# Revit family: P400199-031
name_source: partatom
category: Lighting Fixtures
revit_build: Autodesk Revit 2014 (Build: 20130308_1515(x64)
units: mm (PartAtom-declared; Revit-internal decimal feet)

## types (1)
- P400199-031
    Apparent Load = 60 VA
    Assembly Code = D5020200
    Default Elevation = 48 "
    Description = This versatile chandelier from the Durrell Collection will easily find a home in a variety of settings in need of generous illumination. Light bases reminiscent of vintage candlesticks are coated in a beautiful matte black finish and appear to float around the structure on gently curving metal arms. A wooden column coated in a cerused black finish stretches elegantly at the light fixture’s center to attach the design to a linked metal chain.
    Features = Light bases reminiscent of vintage candlesticks are coated in a beautiful matte black finish.
The light bases appear to float around the structure on gently curving metal arms.
A wooden column coated in a cerused black finish stretches elegantly at the light fixture’s center to attach the design to a linked metal chain.
Ideal for any foyer, hallway, dining room, or kitchen.
Perfect for rustic, farmhouse, and coastal settings.
Measures 26-1/2-inch width by 22-1/2-inch height.
Uses five candelabra base bulbs that are sold separately (60w max - LED or incandescent).
Able to be fully dimmable with dimmable bulbs.
Includes installation instructions and mounting hardware.
Progress Lighting products are designed for exceptional quality, reliability, and functionality.
    Fixture distribution = Direct
    Glass = Paint - Hubbell - White Texture
    Gold = Hubbell - Gold
    Height = 26.5 "
    Housing Material = Paint - Hubbell - Textured Camera Black
    Lamp = LED or Medium Base
    Load Classification = Lighting
    Manufacturer = Progress Lighting
    Model = P400199-031
    Power Factor = 1
    Product Documentation Link = https://hubbellcdn.com
    Product Link = https://www.hubbell.com
    URL = https://www.hubbell.com
    Voltage = 120 V
    Warranty = 1 year Warranty
    Wattage Comments = 60W
    Watts = 60 W
    Width = 6 "

## geometry (parser evidence)
native form markers: Sweep x3
no freeform markers — native parametric forms only
